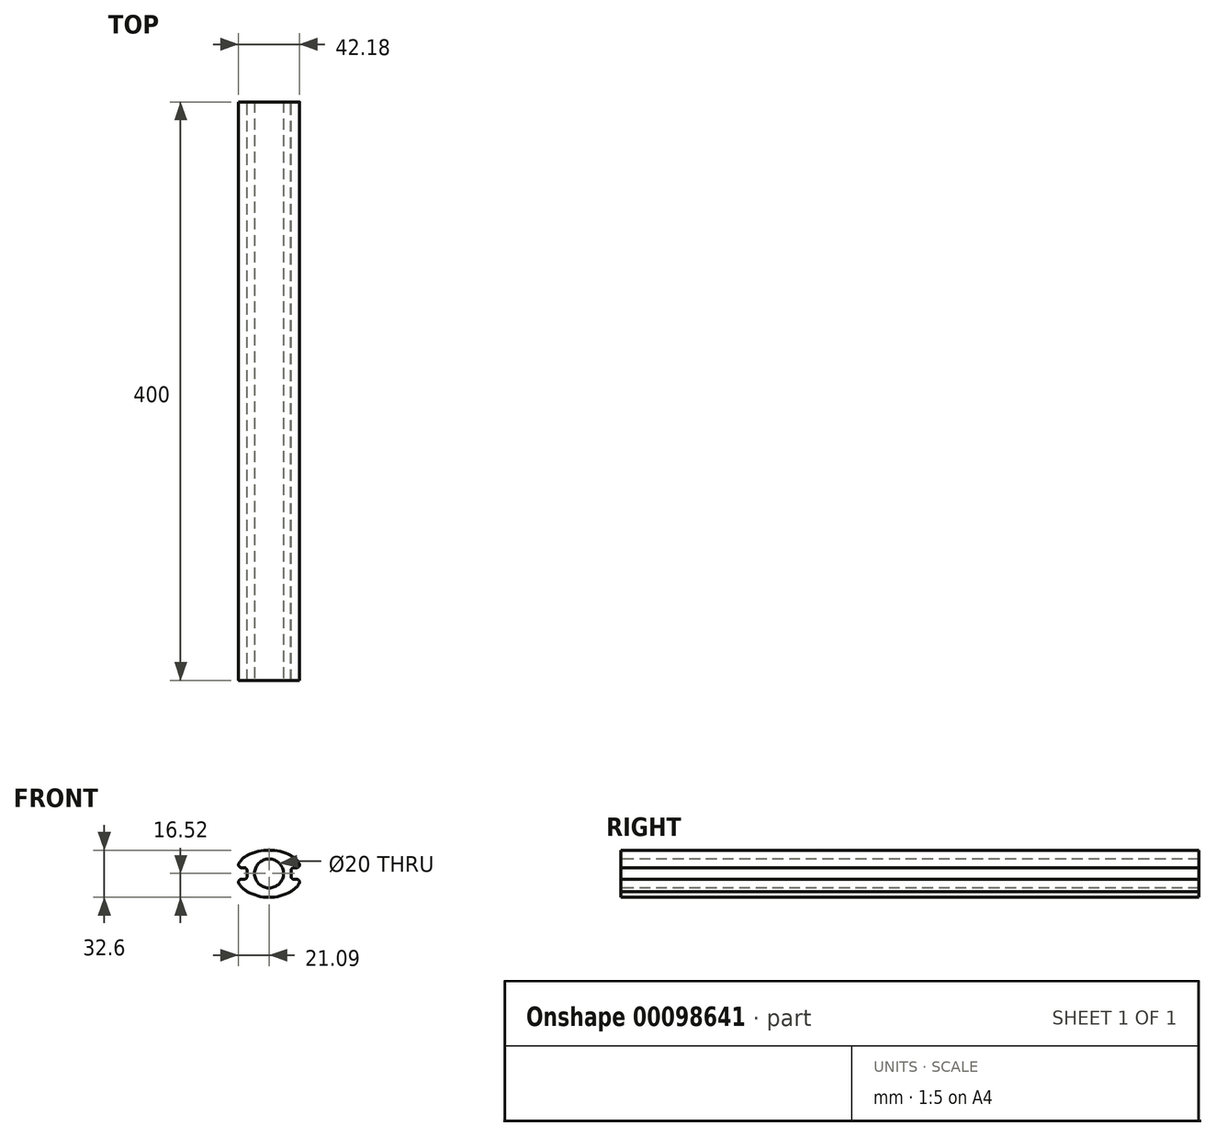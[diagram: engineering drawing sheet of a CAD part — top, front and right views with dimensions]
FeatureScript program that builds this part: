
annotation { "Feature Type Name" : "Feature", "Feature Type Description" : "" }
export const myFeature = defineFeature(function(context is Context, id is Id, definition is map)
    precondition{}
    {
        {
            var Q0;
            Q0=qCreatedBy(makeId("Front.planeOp"),FACE);
            var sketch = newSketch(context, id + "F0", { "sketchPlane" : qUnion([Q0])});
            skLineSegment(sketch, "E0.bottom", {"start": v(15, 12.5) * mm, "end": v(-15, 12.5) * mm});
            skLineSegment(sketch, "E0.top", {"start": v(15, -12.5) * mm, "end": v(-15, -12.5) * mm});
            skLineSegment(sketch, "E0.left", {"start": v(15, 12.5) * mm, "end": v(15, -12.5) * mm});
            skLineSegment(sketch, "E0.right", {"start": v(-15, 12.5) * mm, "end": v(-15, -12.5) * mm});
            skPoint(sketch, "E0.middle", {"position": v(0, 0) * mm});
            skArc(sketch, "E1", {"start": v(15, 12.5) * mm, "mid": v(0, 16.08) * mm, "end": v(-15, 12.5) * mm});
            skArc(sketch, "E2", {"start": v(-15, 12.5) * mm, "mid": v(-22.7, 0) * mm, "end": v(-15, -12.5) * mm});
            skArc(sketch, "E3", {"start": v(15, -12.5) * mm, "mid": v(22.7, 0) * mm, "end": v(15, 12.5) * mm});
            skArc(sketch, "E4", {"start": v(-15, -12.5) * mm, "mid": v(0, -16.52) * mm, "end": v(15, -12.5) * mm});
            skLineSegment(sketch, "E5.bottom", {"start": v(-15.2, 4) * mm, "end": v(-30.2, 4) * mm});
            skLineSegment(sketch, "E5.top", {"start": v(-15.2, -4) * mm, "end": v(-30.2, -4) * mm});
            skLineSegment(sketch, "E5.left", {"start": v(-15.2, 4) * mm, "end": v(-15.2, -4) * mm});
            skLineSegment(sketch, "E5.right", {"start": v(-30.2, 4) * mm, "end": v(-30.2, -4) * mm});
            skPoint(sketch, "E5.middle", {"position": v(-22.7, 0) * mm});
            skLineSegment(sketch, "E6.bottom", {"start": v(30.2, 4) * mm, "end": v(15.2, 4) * mm});
            skLineSegment(sketch, "E6.top", {"start": v(30.2, -4) * mm, "end": v(15.2, -4) * mm});
            skLineSegment(sketch, "E6.left", {"start": v(30.2, 4) * mm, "end": v(30.2, -4) * mm});
            skLineSegment(sketch, "E6.right", {"start": v(15.2, 4) * mm, "end": v(15.2, -4) * mm});
            skPoint(sketch, "E6.middle", {"position": v(22.7, 0) * mm});
            skSolve(sketch);
        }
        {
            var Q0;
            Q0=makeQuery(id+"F0.imprint","IMPRINT",FACE,{"disambiguationData":[TD([[makeQuery(id+"F0.imprint","IMPRINT",EDGE,{"derivedFrom":sQuery(id+"F0.wireOp",EDGE,"E0.bottom")}),1.0]])]});
            var Q1;
            {var subQ4=sQuery(id+"F0.wireOp",EDGE,"E0.right");Q1=makeQuery(id+"F0.imprint","IMPRINT",FACE,{"disambiguationData":[TD([[makeQuery(id+"F0.imprint","IMPRINT",EDGE,{"derivedFrom":subQ4}),-1.0]])]});}
            var Q2;
            Q2=makeQuery(id+"F0.imprint","IMPRINT",FACE,{"disambiguationData":[TD([[makeQuery(id+"F0.imprint","IMPRINT",EDGE,{"derivedFrom":sQuery(id+"F0.wireOp",EDGE,"E0.top")}),1.0]])]});
            var Q3;
            {var subQ4=sQuery(id+"F0.wireOp",EDGE,"E0.left");Q3=makeQuery(id+"F0.imprint","IMPRINT",FACE,{"disambiguationData":[TD([[makeQuery(id+"F0.imprint","IMPRINT",EDGE,{"derivedFrom":subQ4}),1.0]])]});}
            var Q4;
            Q4=makeQuery(id+"F0.imprint","IMPRINT",FACE,{"disambiguationData":[TD([[makeQuery(id+"F0.imprint","IMPRINT",EDGE,{"derivedFrom":sQuery(id+"F0.wireOp",EDGE,"E0.bottom")}),-1.0]])]});
            extrude(context, id + "F1", {"entities" : qUnion([Q0, Q1, Q2, Q3, Q4]), "depth" : 400 * mm});
        }
        {
            var Q0;
            Q0=makeQuery(id+"F1.opExtrude","SWEPT_EDGE",EDGE,{"disambiguationData":[OSD([sQuery(id+"F0.wireOp",EDGE,"E2"),sQuery(id+"F0.wireOp",EDGE,"E5.bottom")])]});
            var Q1;
            Q1=makeQuery(id+"F1.opExtrude","SWEPT_EDGE",EDGE,{"disambiguationData":[OSD([sQuery(id+"F0.wireOp",EDGE,"E5.bottom"),sQuery(id+"F0.wireOp",EDGE,"E5.left")])]});
            var Q2;
            Q2=makeQuery(id+"F1.opExtrude","SWEPT_EDGE",EDGE,{"disambiguationData":[OSD([sQuery(id+"F0.wireOp",EDGE,"E5.top"),sQuery(id+"F0.wireOp",EDGE,"E5.left")])]});
            var Q3;
            Q3=makeQuery(id+"F1.opExtrude","SWEPT_EDGE",EDGE,{"disambiguationData":[OSD([sQuery(id+"F0.wireOp",EDGE,"E2"),sQuery(id+"F0.wireOp",EDGE,"E5.top")])]});
            var Q4;
            Q4=makeQuery(id+"F1.opExtrude","SWEPT_EDGE",EDGE,{"disambiguationData":[OSD([sQuery(id+"F0.wireOp",EDGE,"E6.top"),sQuery(id+"F0.wireOp",EDGE,"E6.right")])]});
            var Q5;
            Q5=makeQuery(id+"F1.opExtrude","SWEPT_EDGE",EDGE,{"disambiguationData":[OSD([sQuery(id+"F0.wireOp",EDGE,"E3"),sQuery(id+"F0.wireOp",EDGE,"E6.bottom")])]});
            var Q6;
            Q6=makeQuery(id+"F1.opExtrude","SWEPT_EDGE",EDGE,{"disambiguationData":[OSD([sQuery(id+"F0.wireOp",EDGE,"E6.bottom"),sQuery(id+"F0.wireOp",EDGE,"E6.right")])]});
            var Q7;
            Q7=makeQuery(id+"F1.opExtrude","SWEPT_EDGE",EDGE,{"disambiguationData":[OSD([sQuery(id+"F0.wireOp",EDGE,"E3"),sQuery(id+"F0.wireOp",EDGE,"E6.top")])]});
            fillet(context, id + "F2", {"entities" : qUnion([Q0, Q1, Q2, Q3, Q4, Q5, Q6, Q7]), "radius" : 2 * mm, "tangentPropagation" : true, "allowEdgeOverflow" : false});
        }
        {
            var Q0;
            Q0=makeQuery(id+"F1.opExtrude","CAP_FACE",FACE,{"disambiguationData":[OSD([sQuery(id+"F0.wireOp",EDGE,"E1"),sQuery(id+"F0.wireOp",EDGE,"E2"),sQuery(id+"F0.wireOp",EDGE,"E3"),sQuery(id+"F0.wireOp",EDGE,"E4"),sQuery(id+"F0.wireOp",EDGE,"E5.bottom"),sQuery(id+"F0.wireOp",EDGE,"E5.top"),sQuery(id+"F0.wireOp",EDGE,"E5.left"),sQuery(id+"F0.wireOp",EDGE,"E6.bottom"),sQuery(id+"F0.wireOp",EDGE,"E6.top"),sQuery(id+"F0.wireOp",EDGE,"E6.right")])],"isStart":false});
            var sketch = newSketch(context, id + "F3", { "sketchPlane" : qUnion([Q0])});
            skCircle(sketch, "E7", {"center": v(0, 0) * mm, "radius": 10 * mm});
            skSolve(sketch);
        }
        {
            var Q0;
            Q0=makeQuery(id+"F3.imprint","IMPRINT",FACE,{"disambiguationData":[TD([[makeQuery(id+"F3.imprint","IMPRINT",EDGE,{"derivedFrom":sQuery(id+"F3.wireOp",EDGE,"E7")}),1.0]])]});
            extrude(context, id + "F4", {"entities" : qUnion([Q0]), "operationType" : NewBodyOperationType.REMOVE, "oppositeDirection" : true, "depth" : 400 * mm});
        }
    });
